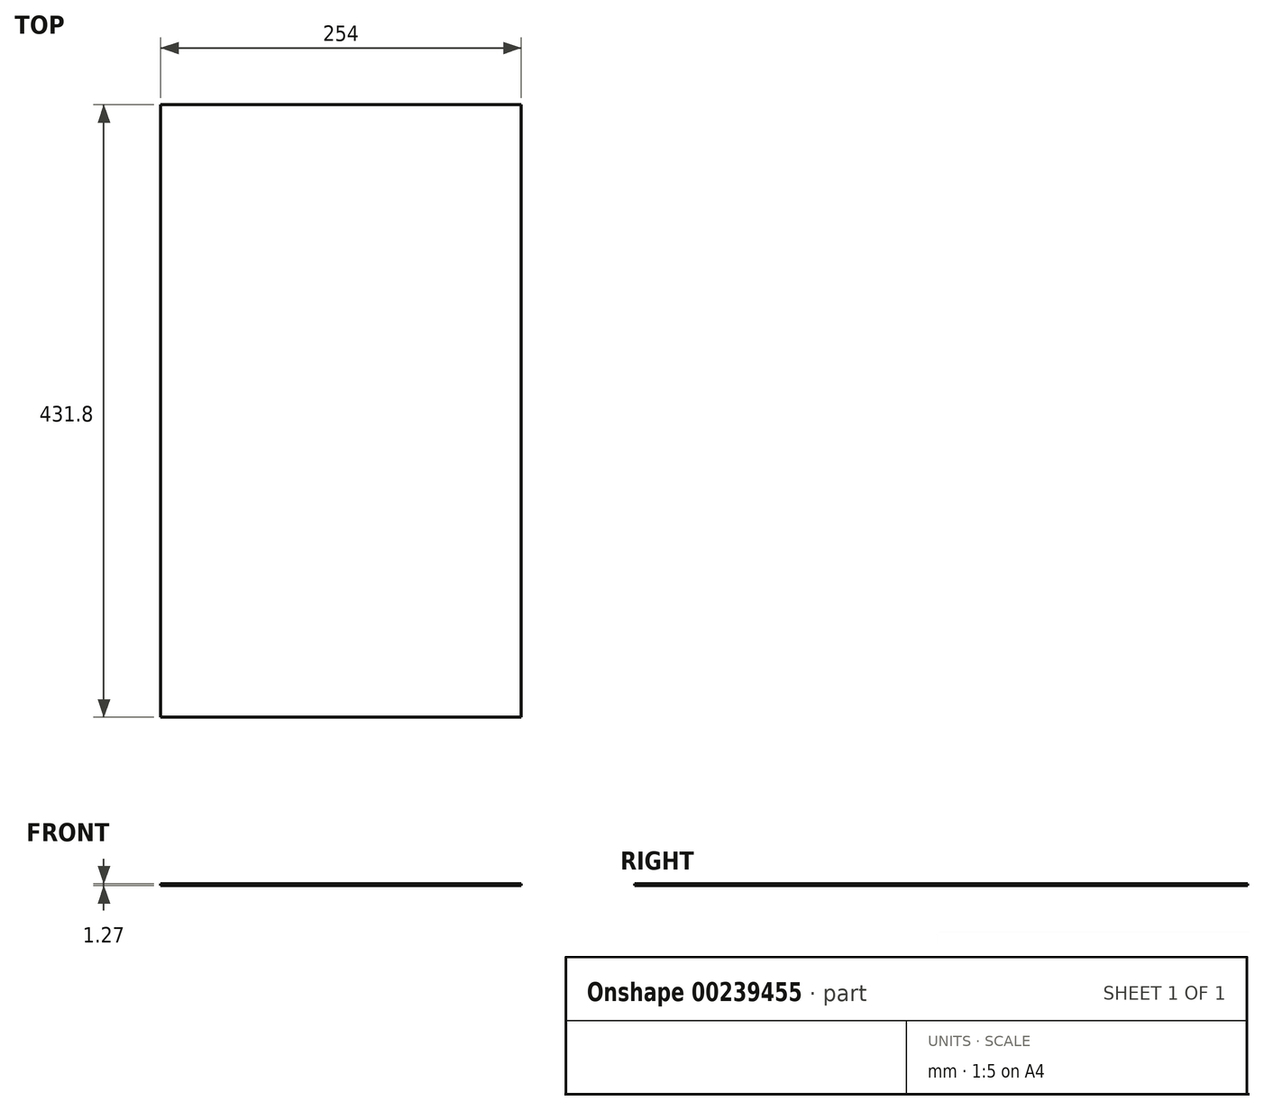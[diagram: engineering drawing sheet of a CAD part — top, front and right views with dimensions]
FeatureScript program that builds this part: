
annotation { "Feature Type Name" : "Feature", "Feature Type Description" : "" }
export const myFeature = defineFeature(function(context is Context, id is Id, definition is map)
    precondition{}
    {
        {
            var Q0;
            Q0=qCreatedBy(makeId("Top.planeOp"),FACE);
            var sketch = newSketch(context, id + "F0", { "sketchPlane" : qUnion([Q0])});
            skLineSegment(sketch, "E0.bottom", {"start": v(-127, 215.9) * mm, "end": v(127, 215.9) * mm});
            skLineSegment(sketch, "E0.top", {"start": v(-127, -215.9) * mm, "end": v(127, -215.9) * mm});
            skLineSegment(sketch, "E0.left", {"start": v(-127, 215.9) * mm, "end": v(-127, -215.9) * mm});
            skLineSegment(sketch, "E0.right", {"start": v(127, 215.9) * mm, "end": v(127, -215.9) * mm});
            skPoint(sketch, "E0.middle", {"position": v(0, 0) * mm});
            skSolve(sketch);
        }
        {
            var Q0;
            Q0 = qSketchRegion(id + "F0", true);
            extrude(context, id + "F1", {"entities" : qUnion([Q0]), "depth" : 1.27 * mm});
        }
    });
